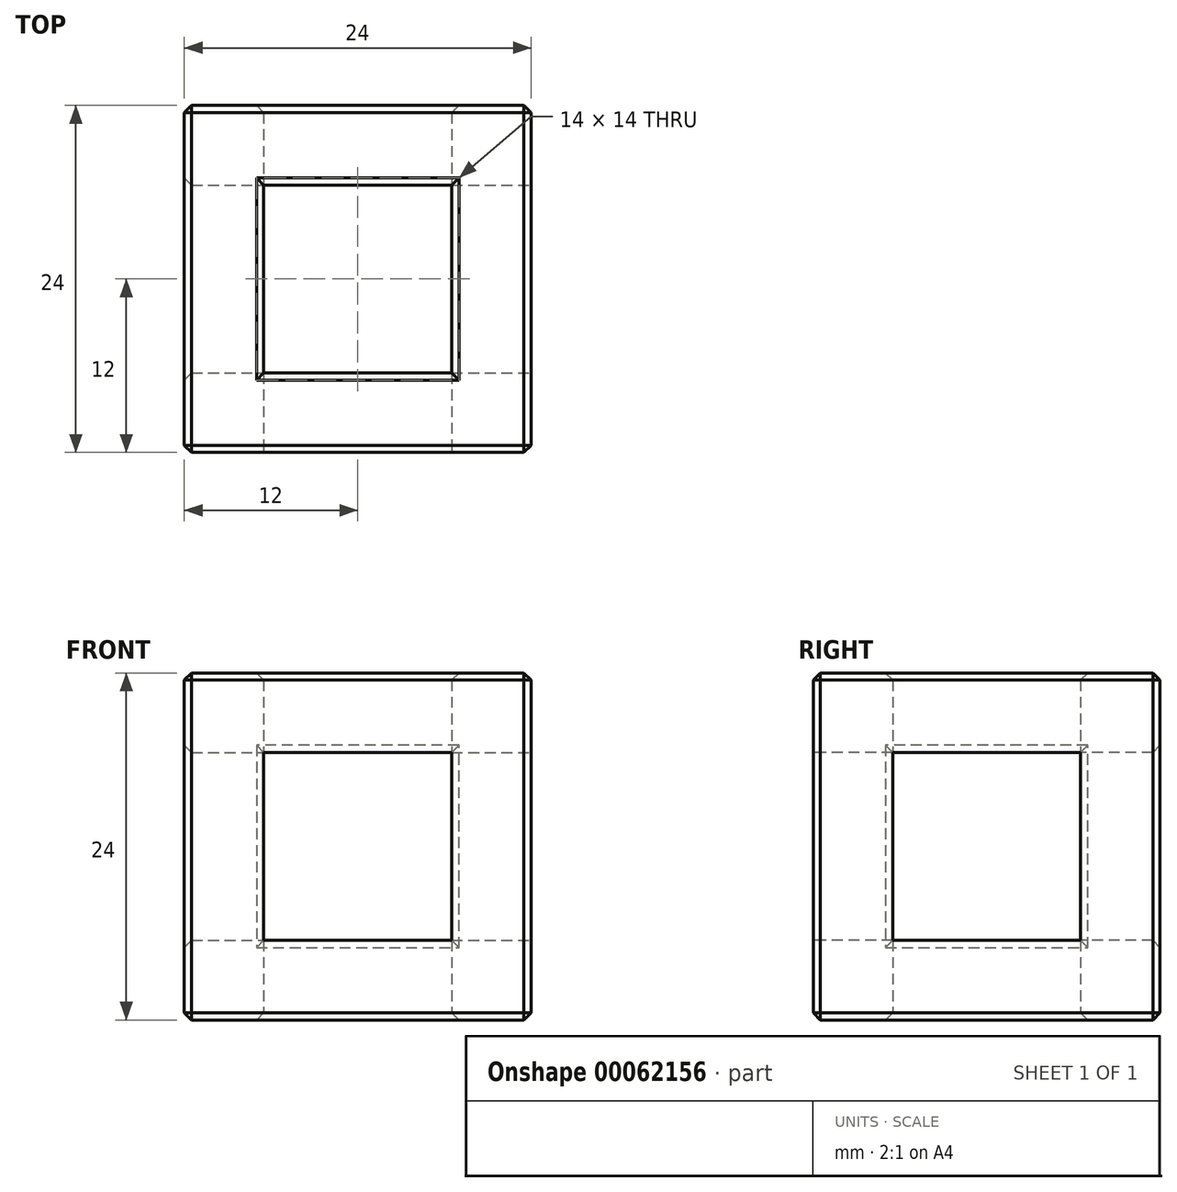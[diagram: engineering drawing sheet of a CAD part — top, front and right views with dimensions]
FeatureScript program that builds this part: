
annotation { "Feature Type Name" : "Feature", "Feature Type Description" : "" }
export const myFeature = defineFeature(function(context is Context, id is Id, definition is map)
    precondition{}
    {
        {
            var Q0;
            Q0=qCreatedBy(makeId("Top.planeOp"),FACE);
            var sketch = newSketch(context, id + "F0", { "sketchPlane" : qUnion([Q0])});
            skLineSegment(sketch, "E0.rect.bottom", {"start": v(12, 12) * mm, "end": v(-12, 12) * mm});
            skLineSegment(sketch, "E0.rect.top", {"start": v(12, -12) * mm, "end": v(-12, -12) * mm});
            skLineSegment(sketch, "E0.rect.left", {"start": v(12, 12) * mm, "end": v(12, -12) * mm});
            skLineSegment(sketch, "E0.rect.right", {"start": v(-12, 12) * mm, "end": v(-12, -12) * mm});
            skPoint(sketch, "E0.rect.middle", {"position": v(0, 0) * mm});
            skLineSegment(sketch, "E1.rect.bottom", {"start": v(6.5, 6.5) * mm, "end": v(-6.5, 6.5) * mm});
            skLineSegment(sketch, "E1.rect.top", {"start": v(6.5, -6.5) * mm, "end": v(-6.5, -6.5) * mm});
            skLineSegment(sketch, "E1.rect.left", {"start": v(6.5, 6.5) * mm, "end": v(6.5, -6.5) * mm});
            skLineSegment(sketch, "E1.rect.right", {"start": v(-6.5, 6.5) * mm, "end": v(-6.5, -6.5) * mm});
            skSolve(sketch);
        }
        {
            var Q0;
            Q0=makeQuery(id+"F0.imprint","IMPRINT",FACE,{"disambiguationData":[TD([[makeQuery(id+"F0.imprint","IMPRINT",EDGE,{"derivedFrom":sQuery(id+"F0.wireOp",EDGE,"E0.rect.bottom")}),1.0]])]});
            extrude(context, id + "F1", {"entities" : qUnion([Q0]), "depth" : 12 * mm, "hasSecondDirection" : true, "secondDirectionOppositeDirection" : true, "secondDirectionDepth" : 12 * mm});
        }
        {
            var Q0;
            Q0=makeQuery(id+"F1.opExtrude","SWEPT_FACE",FACE,{"disambiguationData":[OSD([sQuery(id+"F0.wireOp",EDGE,"E0.rect.top")])]});
            var sketch = newSketch(context, id + "F2", { "sketchPlane" : qUnion([Q0])});
            skLineSegment(sketch, "E2.rect.bottom", {"start": v(6.5, 6.5) * mm, "end": v(-6.5, 6.5) * mm});
            skLineSegment(sketch, "E2.rect.top", {"start": v(6.5, -6.5) * mm, "end": v(-6.5, -6.5) * mm});
            skLineSegment(sketch, "E2.rect.left", {"start": v(6.5, 6.5) * mm, "end": v(6.5, -6.5) * mm});
            skLineSegment(sketch, "E2.rect.right", {"start": v(-6.5, 6.5) * mm, "end": v(-6.5, -6.5) * mm});
            skPoint(sketch, "E2.rect.middle", {"position": v(0, 0) * mm});
            skSolve(sketch);
        }
        {
            var Q0;
            Q0=makeQuery(id+"F2.imprint","IMPRINT",FACE,{"disambiguationData":[TD([[makeQuery(id+"F2.imprint","IMPRINT",EDGE,{"derivedFrom":sQuery(id+"F2.wireOp",EDGE,"E2.rect.bottom")}),1.0]])]});
            extrude(context, id + "F3", {"entities" : qUnion([Q0]), "operationType" : NewBodyOperationType.REMOVE, "endBound" : BoundingType.THROUGH_ALL, "oppositeDirection" : true, "depth" : 25 * mm});
        }
        {
            var Q0;
            Q0=makeQuery(id+"F1.opExtrude","SWEPT_FACE",FACE,{"disambiguationData":[OSD([sQuery(id+"F0.wireOp",EDGE,"E0.rect.left")])]});
            var sketch = newSketch(context, id + "F4", { "sketchPlane" : qUnion([Q0])});
            skLineSegment(sketch, "E3.rect.bottom", {"start": v(6.5, 6.5) * mm, "end": v(-6.5, 6.5) * mm});
            skLineSegment(sketch, "E3.rect.top", {"start": v(6.5, -6.5) * mm, "end": v(-6.5, -6.5) * mm});
            skLineSegment(sketch, "E3.rect.left", {"start": v(6.5, 6.5) * mm, "end": v(6.5, -6.5) * mm});
            skLineSegment(sketch, "E3.rect.right", {"start": v(-6.5, 6.5) * mm, "end": v(-6.5, -6.5) * mm});
            skPoint(sketch, "E3.rect.middle", {"position": v(0, 0) * mm});
            skSolve(sketch);
        }
        {
            var Q0;
            Q0=makeQuery(id+"F4.imprint","IMPRINT",FACE,{"disambiguationData":[TD([[makeQuery(id+"F4.imprint","IMPRINT",EDGE,{"derivedFrom":sQuery(id+"F4.wireOp",EDGE,"E3.rect.bottom")}),1.0]])]});
            extrude(context, id + "F5", {"entities" : qUnion([Q0]), "operationType" : NewBodyOperationType.REMOVE, "endBound" : BoundingType.THROUGH_ALL, "oppositeDirection" : true, "depth" : 25 * mm});
        }
        {
            var Q0;
            Q0=makeQuery(id+"F1.opExtrude","CAP_EDGE",EDGE,{"disambiguationData":[OSD([sQuery(id+"F0.wireOp",EDGE,"E0.rect.right")])],"isStart":false});
            var Q1;
            Q1=makeQuery(id+"F1.opExtrude","SWEPT_EDGE",EDGE,{"disambiguationData":[OSD([sQuery(id+"F0.wireOp",EDGE,"E0.rect.bottom"),sQuery(id+"F0.wireOp",EDGE,"E0.rect.right")])]});
            var Q2;
            Q2=makeQuery(id+"F1.opExtrude","CAP_EDGE",EDGE,{"disambiguationData":[OSD([sQuery(id+"F0.wireOp",EDGE,"E0.rect.right")])],"isStart":true});
            var Q3;
            Q3=makeQuery(id+"F1.opExtrude","SWEPT_EDGE",EDGE,{"disambiguationData":[OSD([sQuery(id+"F0.wireOp",EDGE,"E0.rect.top"),sQuery(id+"F0.wireOp",EDGE,"E0.rect.right")])]});
            var Q4;
            Q4=makeQuery(id+"F1.opExtrude","CAP_EDGE",EDGE,{"disambiguationData":[OSD([sQuery(id+"F0.wireOp",EDGE,"E0.rect.left")])],"isStart":false});
            var Q5;
            Q5=makeQuery(id+"F1.opExtrude","SWEPT_EDGE",EDGE,{"disambiguationData":[OSD([sQuery(id+"F0.wireOp",EDGE,"E0.rect.bottom"),sQuery(id+"F0.wireOp",EDGE,"E0.rect.left")])]});
            var Q6;
            Q6=makeQuery(id+"F1.opExtrude","CAP_EDGE",EDGE,{"disambiguationData":[OSD([sQuery(id+"F0.wireOp",EDGE,"E0.rect.left")])],"isStart":true});
            var Q7;
            Q7=makeQuery(id+"F1.opExtrude","SWEPT_EDGE",EDGE,{"disambiguationData":[OSD([sQuery(id+"F0.wireOp",EDGE,"E0.rect.top"),sQuery(id+"F0.wireOp",EDGE,"E0.rect.left")])]});
            var Q8;
            Q8=makeQuery(id+"F1.opExtrude","CAP_EDGE",EDGE,{"disambiguationData":[OSD([sQuery(id+"F0.wireOp",EDGE,"E0.rect.bottom")])],"isStart":true});
            var Q9;
            Q9=makeQuery(id+"F1.opExtrude","CAP_EDGE",EDGE,{"disambiguationData":[OSD([sQuery(id+"F0.wireOp",EDGE,"E0.rect.bottom")])],"isStart":false});
            var Q10;
            Q10=makeQuery(id+"F1.opExtrude","CAP_EDGE",EDGE,{"disambiguationData":[OSD([sQuery(id+"F0.wireOp",EDGE,"E0.rect.top")])],"isStart":true});
            var Q11;
            Q11=makeQuery(id+"F1.opExtrude","CAP_EDGE",EDGE,{"disambiguationData":[OSD([sQuery(id+"F0.wireOp",EDGE,"E0.rect.top")])],"isStart":false});
            var Q12;
            Q12=makeQuery(id+"F1.opExtrude","CAP_EDGE",EDGE,{"disambiguationData":[OSD([sQuery(id+"F0.wireOp",EDGE,"E1.rect.left")])],"isStart":false});
            var Q13;
            Q13=makeQuery(id+"F1.opExtrude","CAP_EDGE",EDGE,{"disambiguationData":[OSD([sQuery(id+"F0.wireOp",EDGE,"E1.rect.bottom")])],"isStart":false});
            var Q14;
            Q14=makeQuery(id+"F1.opExtrude","CAP_EDGE",EDGE,{"disambiguationData":[OSD([sQuery(id+"F0.wireOp",EDGE,"E1.rect.right")])],"isStart":false});
            var Q15;
            Q15=makeQuery(id+"F1.opExtrude","CAP_EDGE",EDGE,{"disambiguationData":[OSD([sQuery(id+"F0.wireOp",EDGE,"E1.rect.top")])],"isStart":false});
            var Q16;
            Q16=makeQuery(id+"F3.boolean.opBoolean","COPY",EDGE,{"derivedFrom":makeQuery(id+"F3.opExtrude","CAP_EDGE",EDGE,{"disambiguationData":[OSD([sQuery(id+"F2.wireOp",EDGE,"E2.rect.left")])],"isStart":true})});
            var Q17;
            Q17=makeQuery(id+"F3.boolean.opBoolean","COPY",EDGE,{"derivedFrom":makeQuery(id+"F3.opExtrude","CAP_EDGE",EDGE,{"disambiguationData":[OSD([sQuery(id+"F2.wireOp",EDGE,"E2.rect.bottom")])],"isStart":true})});
            var Q18;
            Q18=makeQuery(id+"F3.boolean.opBoolean","COPY",EDGE,{"derivedFrom":makeQuery(id+"F3.opExtrude","CAP_EDGE",EDGE,{"disambiguationData":[OSD([sQuery(id+"F2.wireOp",EDGE,"E2.rect.right")])],"isStart":true})});
            var Q19;
            Q19=makeQuery(id+"F3.boolean.opBoolean","COPY",EDGE,{"derivedFrom":makeQuery(id+"F3.opExtrude","CAP_EDGE",EDGE,{"disambiguationData":[OSD([sQuery(id+"F2.wireOp",EDGE,"E2.rect.top")])],"isStart":true})});
            var Q20;
            Q20=makeQuery(id+"F5.boolean.opBoolean","COPY",EDGE,{"derivedFrom":makeQuery(id+"F5.opExtrude","CAP_EDGE",EDGE,{"disambiguationData":[OSD([sQuery(id+"F4.wireOp",EDGE,"E3.rect.right")])],"isStart":true})});
            var Q21;
            Q21=makeQuery(id+"F5.boolean.opBoolean","COPY",EDGE,{"derivedFrom":makeQuery(id+"F5.opExtrude","CAP_EDGE",EDGE,{"disambiguationData":[OSD([sQuery(id+"F4.wireOp",EDGE,"E3.rect.bottom")])],"isStart":true})});
            var Q22;
            Q22=makeQuery(id+"F5.boolean.opBoolean","COPY",EDGE,{"derivedFrom":makeQuery(id+"F5.opExtrude","CAP_EDGE",EDGE,{"disambiguationData":[OSD([sQuery(id+"F4.wireOp",EDGE,"E3.rect.left")])],"isStart":true})});
            var Q23;
            Q23=makeQuery(id+"F5.boolean.opBoolean","COPY",EDGE,{"derivedFrom":makeQuery(id+"F5.opExtrude","CAP_EDGE",EDGE,{"disambiguationData":[OSD([sQuery(id+"F4.wireOp",EDGE,"E3.rect.top")])],"isStart":true})});
            var Q24;
            Q24=makeQuery(id+"F3.boolean.opBoolean","INTERSECT",EDGE,{"derivedFrom":[makeQuery(id+"F1.opExtrude","SWEPT_FACE",FACE,{"disambiguationData":[OSD([sQuery(id+"F0.wireOp",EDGE,"E0.rect.bottom")])]}),makeQuery(id+"F3.opExtrude","SWEPT_FACE",FACE,{"disambiguationData":[OSD([sQuery(id+"F2.wireOp",EDGE,"E2.rect.left")])]})]});
            var Q25;
            Q25=makeQuery(id+"F3.boolean.opBoolean","INTERSECT",EDGE,{"derivedFrom":[makeQuery(id+"F1.opExtrude","SWEPT_FACE",FACE,{"disambiguationData":[OSD([sQuery(id+"F0.wireOp",EDGE,"E0.rect.bottom")])]}),makeQuery(id+"F3.opExtrude","SWEPT_FACE",FACE,{"disambiguationData":[OSD([sQuery(id+"F2.wireOp",EDGE,"E2.rect.bottom")])]})]});
            var Q26;
            Q26=makeQuery(id+"F3.boolean.opBoolean","INTERSECT",EDGE,{"derivedFrom":[makeQuery(id+"F1.opExtrude","SWEPT_FACE",FACE,{"disambiguationData":[OSD([sQuery(id+"F0.wireOp",EDGE,"E0.rect.bottom")])]}),makeQuery(id+"F3.opExtrude","SWEPT_FACE",FACE,{"disambiguationData":[OSD([sQuery(id+"F2.wireOp",EDGE,"E2.rect.right")])]})]});
            var Q27;
            Q27=makeQuery(id+"F3.boolean.opBoolean","INTERSECT",EDGE,{"derivedFrom":[makeQuery(id+"F1.opExtrude","SWEPT_FACE",FACE,{"disambiguationData":[OSD([sQuery(id+"F0.wireOp",EDGE,"E0.rect.bottom")])]}),makeQuery(id+"F3.opExtrude","SWEPT_FACE",FACE,{"disambiguationData":[OSD([sQuery(id+"F2.wireOp",EDGE,"E2.rect.top")])]})]});
            var Q28;
            Q28=makeQuery(id+"F1.opExtrude","CAP_EDGE",EDGE,{"disambiguationData":[OSD([sQuery(id+"F0.wireOp",EDGE,"E1.rect.bottom")])],"isStart":true});
            var Q29;
            Q29=makeQuery(id+"F1.opExtrude","CAP_EDGE",EDGE,{"disambiguationData":[OSD([sQuery(id+"F0.wireOp",EDGE,"E1.rect.left")])],"isStart":true});
            var Q30;
            Q30=makeQuery(id+"F1.opExtrude","CAP_EDGE",EDGE,{"disambiguationData":[OSD([sQuery(id+"F0.wireOp",EDGE,"E1.rect.top")])],"isStart":true});
            var Q31;
            Q31=makeQuery(id+"F1.opExtrude","CAP_EDGE",EDGE,{"disambiguationData":[OSD([sQuery(id+"F0.wireOp",EDGE,"E1.rect.right")])],"isStart":true});
            var Q32;
            Q32=makeQuery(id+"F5.boolean.opBoolean","INTERSECT",EDGE,{"derivedFrom":[makeQuery(id+"F1.opExtrude","SWEPT_FACE",FACE,{"disambiguationData":[OSD([sQuery(id+"F0.wireOp",EDGE,"E0.rect.right")])]}),makeQuery(id+"F5.opExtrude","SWEPT_FACE",FACE,{"disambiguationData":[OSD([sQuery(id+"F4.wireOp",EDGE,"E3.rect.top")])]})]});
            var Q33;
            Q33=makeQuery(id+"F5.boolean.opBoolean","INTERSECT",EDGE,{"derivedFrom":[makeQuery(id+"F1.opExtrude","SWEPT_FACE",FACE,{"disambiguationData":[OSD([sQuery(id+"F0.wireOp",EDGE,"E0.rect.right")])]}),makeQuery(id+"F5.opExtrude","SWEPT_FACE",FACE,{"disambiguationData":[OSD([sQuery(id+"F4.wireOp",EDGE,"E3.rect.left")])]})]});
            var Q34;
            Q34=makeQuery(id+"F5.boolean.opBoolean","INTERSECT",EDGE,{"derivedFrom":[makeQuery(id+"F1.opExtrude","SWEPT_FACE",FACE,{"disambiguationData":[OSD([sQuery(id+"F0.wireOp",EDGE,"E0.rect.right")])]}),makeQuery(id+"F5.opExtrude","SWEPT_FACE",FACE,{"disambiguationData":[OSD([sQuery(id+"F4.wireOp",EDGE,"E3.rect.bottom")])]})]});
            var Q35;
            Q35=makeQuery(id+"F5.boolean.opBoolean","INTERSECT",EDGE,{"derivedFrom":[makeQuery(id+"F1.opExtrude","SWEPT_FACE",FACE,{"disambiguationData":[OSD([sQuery(id+"F0.wireOp",EDGE,"E0.rect.right")])]}),makeQuery(id+"F5.opExtrude","SWEPT_FACE",FACE,{"disambiguationData":[OSD([sQuery(id+"F4.wireOp",EDGE,"E3.rect.right")])]})]});
            chamfer(context, id + "F6", {"entities" : qUnion([Q0, Q1, Q2, Q3, Q4, Q5, Q6, Q7, Q8, Q9, Q10, Q11, Q12, Q13, Q14, Q15, Q16, Q17, Q18, Q19, Q20, Q21, Q22, Q23, Q24, Q25, Q26, Q27, Q28, Q29, Q30, Q31, Q32, Q33, Q34, Q35]), "width" : .5 * mm, "tangentPropagation" : true});
        }
    });
